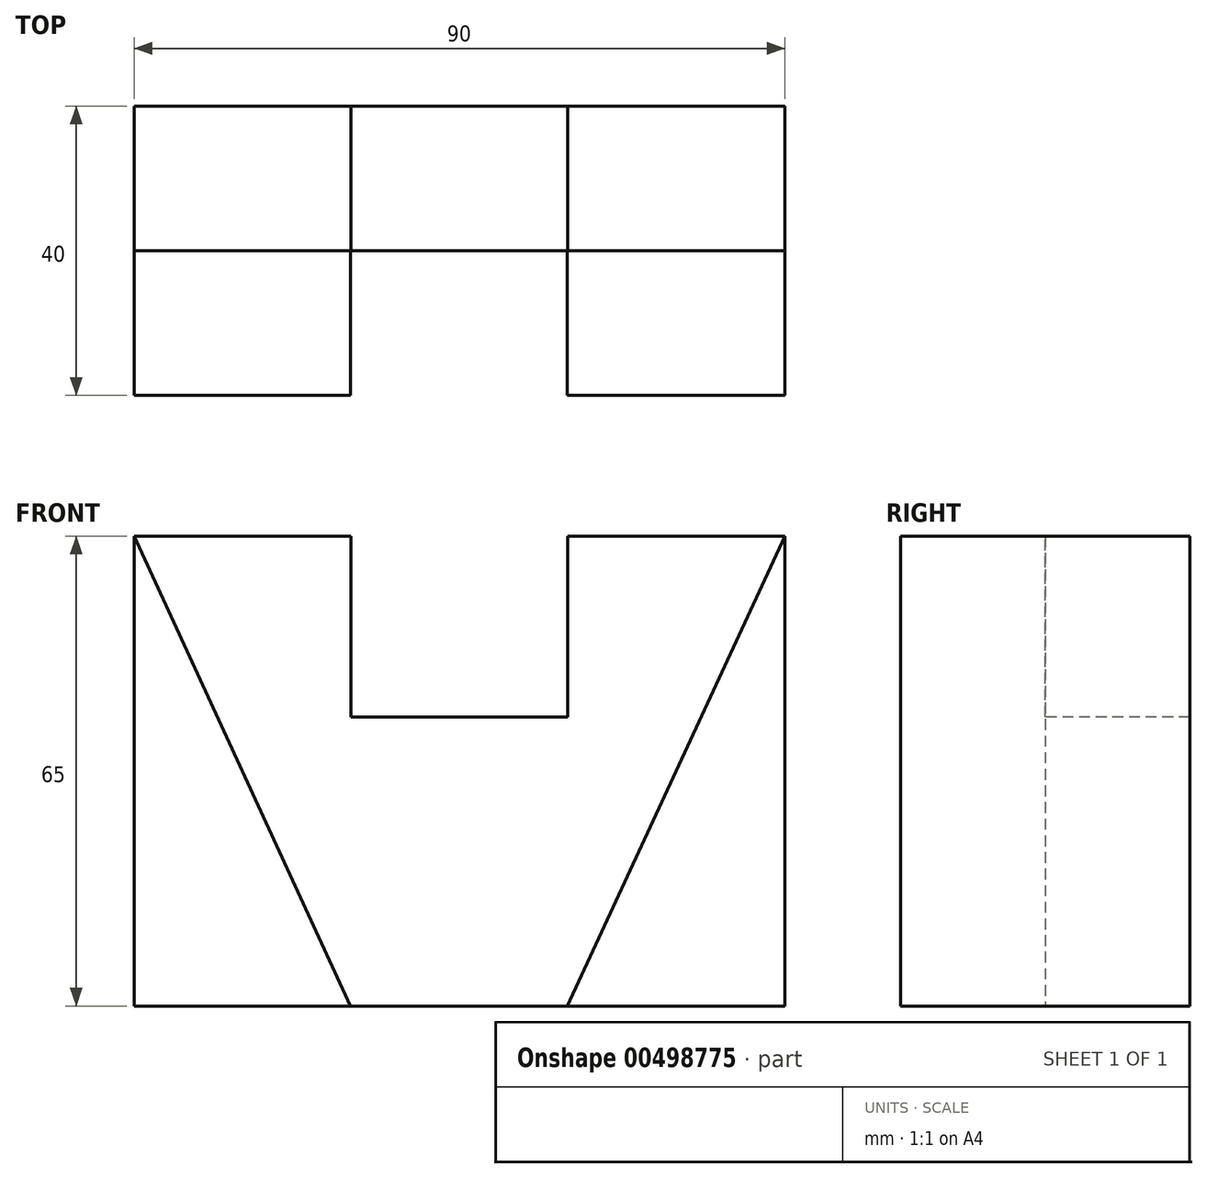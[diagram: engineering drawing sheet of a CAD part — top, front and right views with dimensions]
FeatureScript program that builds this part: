
annotation { "Feature Type Name" : "Feature", "Feature Type Description" : "" }
export const myFeature = defineFeature(function(context is Context, id is Id, definition is map)
    precondition{}
    {
        {
            var Q0;
            Q0=qCreatedBy(makeId("Front.planeOp"),FACE);
            var sketch = newSketch(context, id + "F0", { "sketchPlane" : qUnion([Q0])});
            skLineSegment(sketch, "E0.bottom", {"start": v(45, 32.5) * mm, "end": v(-45, 32.5) * mm});
            skLineSegment(sketch, "E0.top", {"start": v(45, -32.5) * mm, "end": v(-45, -32.5) * mm});
            skLineSegment(sketch, "E0.left", {"start": v(45, 32.5) * mm, "end": v(45, -32.5) * mm});
            skLineSegment(sketch, "E0.right", {"start": v(-45, 32.5) * mm, "end": v(-45, -32.5) * mm});
            skPoint(sketch, "E0.middle", {"position": v(0, 0) * mm});
            skSolve(sketch);
        }
        {
            var Q0;
            Q0=makeQuery(id+"F0.imprint","IMPRINT",FACE,{"disambiguationData":[TD([[makeQuery(id+"F0.imprint","IMPRINT",EDGE,{"derivedFrom":sQuery(id+"F0.wireOp",EDGE,"E0.bottom")}),1.0]])]});
            extrude(context, id + "F1", {"entities" : qUnion([Q0]), "depth" : 20 * mm});
        }
        {
            var Q0;
            Q0=makeQuery(id+"F1.opExtrude","CAP_FACE",FACE,{"disambiguationData":[OSD([sQuery(id+"F0.wireOp",EDGE,"E0.bottom"),sQuery(id+"F0.wireOp",EDGE,"E0.top"),sQuery(id+"F0.wireOp",EDGE,"E0.left"),sQuery(id+"F0.wireOp",EDGE,"E0.right")])],"isStart":false});
            var sketch = newSketch(context, id + "F2", { "sketchPlane" : qUnion([Q0])});
            skLineSegment(sketch, "E1.top", {"start": v(15, 7.5) * mm, "end": v(-15, 7.5) * mm});
            skLineSegment(sketch, "E1.right", {"start": v(-15, 32.5) * mm, "end": v(-15, 7.5) * mm});
            skPoint(sketch, "E1.middle", {"position": v(0, 32.5) * mm});
            skPoint(sketch, "E2.end.orphan", {"position": v(-15, 32.5) * mm});
            skPoint(sketch, "E3.orphan", {"position": v(-15, 57.5) * mm});
            skPoint(sketch, "E1.left.start.orphan", {"position": v(15, 57.5) * mm});
            skLineSegment(sketch, "E4", {"start": v(15, 7.5) * mm, "end": v(15, 32.5) * mm});
            skSolve(sketch);
        }
        {
            var Q0;
            Q0=makeQuery(id+"F2.imprint","IMPRINT",FACE,{"disambiguationData":[TD([[makeQuery(id+"F2.imprint","IMPRINT",EDGE,{"derivedFrom":sQuery(id+"F2.wireOp",EDGE,"E1.top")}),-1.0]])]});
            extrude(context, id + "F3", {"entities" : qUnion([Q0]), "operationType" : NewBodyOperationType.REMOVE, "endBound" : BoundingType.THROUGH_ALL, "oppositeDirection" : true, "depth" : 25 * mm});
        }
        {
            var Q0;
            Q0=makeQuery(id+"F1.opExtrude","CAP_FACE",FACE,{"disambiguationData":[OSD([sQuery(id+"F0.wireOp",EDGE,"E0.bottom"),sQuery(id+"F0.wireOp",EDGE,"E0.top"),sQuery(id+"F0.wireOp",EDGE,"E0.left"),sQuery(id+"F0.wireOp",EDGE,"E0.right")])],"isStart":false});
            var sketch = newSketch(context, id + "F4", { "sketchPlane" : qUnion([Q0])});
            skLineSegment(sketch, "E5", {"start": v(-45, 32.5) * mm, "end": v(-15.06, -32.5) * mm});
            skLineSegment(sketch, "E6", {"start": v(45, 32.5) * mm, "end": v(14.94, -32.5) * mm});
            skSolve(sketch);
        }
        {
            var Q0;
            {var subQ0=sQuery(id+"F4.wireOp",EDGE,"E5");Q0=makeQuery(id+"F4.imprint","IMPRINT",FACE,{"disambiguationData":[TD([[makeQuery(id+"F4.imprint","IMPRINT",EDGE,{"derivedFrom":subQ0}),-1.0]])]});}
            var Q1;
            {var subQ0=sQuery(id+"F4.wireOp",EDGE,"E6");Q1=makeQuery(id+"F4.imprint","IMPRINT",FACE,{"disambiguationData":[TD([[makeQuery(id+"F4.imprint","IMPRINT",EDGE,{"derivedFrom":subQ0}),1.0]])]});}
            extrude(context, id + "F5", {"entities" : qUnion([Q0, Q1]), "operationType" : NewBodyOperationType.ADD, "depth" : 20 * mm});
        }
    });
